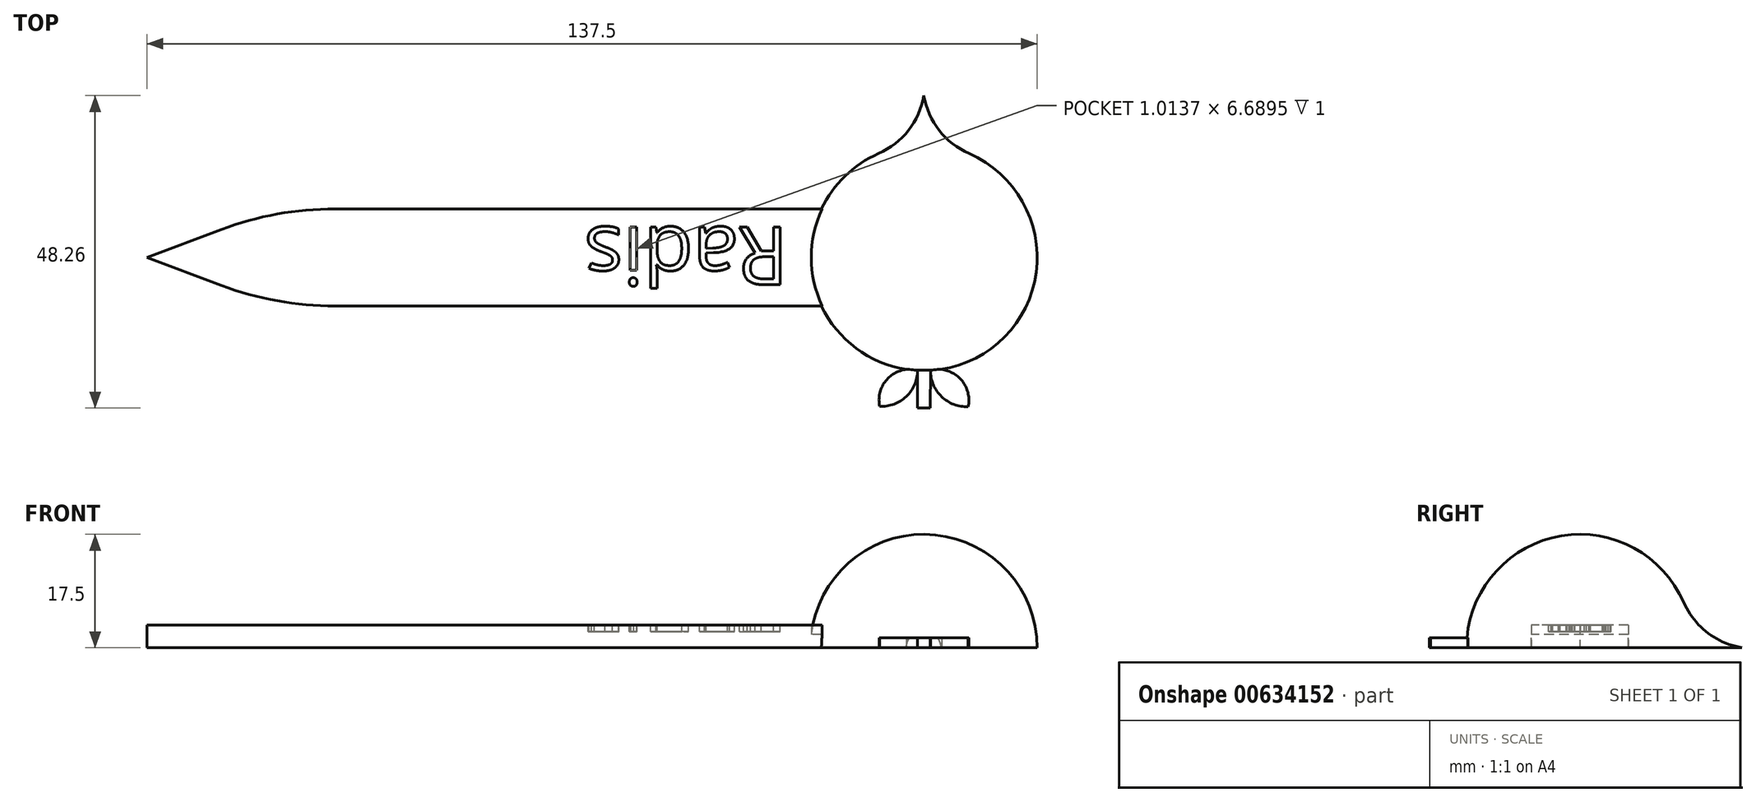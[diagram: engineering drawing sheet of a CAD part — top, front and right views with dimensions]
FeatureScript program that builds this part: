
annotation { "Feature Type Name" : "Feature", "Feature Type Description" : "" }
export const myFeature = defineFeature(function(context is Context, id is Id, definition is map)
    precondition{}
    {
        {
            var Q0;
            Q0=qCreatedBy(makeId("Top.planeOp"),FACE);
            var sketch = newSketch(context, id + "F0", { "sketchPlane" : qUnion([Q0])});
            skLineSegment(sketch, "E0.bottom", {"start": v(20, 7.5) * mm, "end": v(120, 7.5) * mm});
            skLineSegment(sketch, "E0.top", {"start": v(20, -7.5) * mm, "end": v(120, -7.5) * mm});
            skLineSegment(sketch, "E0.left", {"start": v(20, 7.5) * mm, "end": v(20, -7.5) * mm});
            skLineSegment(sketch, "E0.right", {"start": v(120, 7.5) * mm, "end": v(120, -7.5) * mm});
            skLineSegment(sketch, "E1", {"start": v(20, -7.5) * mm, "end": v(0, 0) * mm});
            skPoint(sketch, "E1.endSnap0", {"position": v(20, 0) * mm});
            skLineSegment(sketch, "E2", {"start": v(0, 0) * mm, "end": v(20, 7.5) * mm});
            skSolve(sketch);
        }
        {
            var Q0;
            Q0 = qSketchRegion(id + "F0", true);
            extrude(context, id + "F1", {"entities" : qUnion([Q0]), "depth" : 2 * mm, "offsetDistance" : 25 * mm});
        }
        {
            var Q0;
            Q0=makeQuery(id+"F1.opExtrude","SWEPT_EDGE",EDGE,{"disambiguationData":[OSD([sQuery(id+"F0.wireOp",EDGE,"E0.top"),sQuery(id+"F0.wireOp",EDGE,"E0.left"),sQuery(id+"F0.wireOp",EDGE,"E1")])]});
            var Q1;
            Q1=makeQuery(id+"F1.opExtrude","SWEPT_EDGE",EDGE,{"disambiguationData":[OSD([sQuery(id+"F0.wireOp",EDGE,"E0.bottom"),sQuery(id+"F0.wireOp",EDGE,"E0.left"),sQuery(id+"F0.wireOp",EDGE,"E2")])]});
            fillet(context, id + "F2", {"entities" : qUnion([Q0, Q1]), "radius" : 50 * mm, "tangentPropagation" : true, "allowEdgeOverflow" : false});
        }
        {
            var Q0;
            Q0=makeQuery(id+"F1.opExtrude","CAP_FACE",FACE,{"disambiguationData":[OSD([sQuery(id+"F0.wireOp",EDGE,"E0.bottom"),sQuery(id+"F0.wireOp",EDGE,"E0.top"),sQuery(id+"F0.wireOp",EDGE,"E0.right"),sQuery(id+"F0.wireOp",EDGE,"E1"),sQuery(id+"F0.wireOp",EDGE,"E2")])],"isStart":true});
            var sketch = newSketch(context, id + "F3", { "sketchPlane" : qUnion([Q0])});
            skArc(sketch, "E3", {"start": v(120, 17.5) * mm, "mid": v(102.5, 0) * mm, "end": v(120, -17.5) * mm});
            skLineSegment(sketch, "E4", {"start": v(120, 0) * mm, "end": v(120, -29.85) * mm, "construction": true});
            skArc(sketch, "E5", {"start": v(120, -25) * mm, "mid": v(117.63, -19.63) * mm, "end": v(113, -16.04) * mm});
            skLineSegment(sketch, "E6", {"start": v(120, -25) * mm, "end": v(120, -17.5) * mm});
            skLineSegment(sketch, "E7", {"start": v(120, -17.5) * mm, "end": v(120, 17.5) * mm});
            skSolve(sketch);
        }
        {
            var Q0;
            Q0 = qSketchRegion(id + "F3", true);
            var Q1;
            Q1=sQuery(id+"F3.wireOp",EDGE,"E7");
            revolve(context, id + "F4", {"operationType" : NewBodyOperationType.ADD, "surfaceOperationType" : NewSurfaceOperationType.NEW, "entities" : qUnion([Q0]), "axis" : qUnion([Q1]), "revolveType" : RevolveType.ONE_DIRECTION, "oppositeDirection" : true, "angle" : 180 * degree});
        }
        {
            var Q0;
            Q0=makeQuery(id+"F4.boolean.opBoolean","MERGE",FACE,{"derivedFrom":[makeQuery(id+"F1.opExtrude","CAP_FACE",FACE,{"disambiguationData":[OSD([sQuery(id+"F0.wireOp",EDGE,"E0.bottom"),sQuery(id+"F0.wireOp",EDGE,"E0.top"),sQuery(id+"F0.wireOp",EDGE,"E0.right"),sQuery(id+"F0.wireOp",EDGE,"E1"),sQuery(id+"F0.wireOp",EDGE,"E2")])],"isStart":true}),makeQuery(id+"F4.opRevolve","CAP_FACE",FACE,{"disambiguationData":[OSD([sQuery(id+"F3.wireOp",EDGE,"E3"),sQuery(id+"F3.wireOp",EDGE,"E5"),sQuery(id+"F3.wireOp",EDGE,"E6"),sQuery(id+"F3.wireOp",EDGE,"E7")])],"isStart":true})]});
            var sketch = newSketch(context, id + "F5", { "sketchPlane" : qUnion([Q0])});
            skLineSegment(sketch, "E8", {"start": v(120, 27.39) * mm, "end": v(120.1, -8.4) * mm, "construction": true});
            skLineSegment(sketch, "E9", {"start": v(120.01, 23.26) * mm, "end": v(119.01, 23.25) * mm});
            skLineSegment(sketch, "E10", {"start": v(119.01, 23.25) * mm, "end": v(119.03, 17.47) * mm});
            skArc(sketch, "E11", {"start": v(119.03, 17.47) * mm, "mid": v(117.3, 21.5) * mm, "end": v(113.18, 23) * mm});
            skArc(sketch, "E12", {"start": v(113.18, 23) * mm, "mid": v(113.98, 19.23) * mm, "end": v(117.3, 17.3) * mm});
            skLineSegment(sketch, "E13.MirrorCS", {"start": v(120.01, 23.26) * mm, "end": v(121.01, 23.26) * mm});
            skLineSegment(sketch, "E14.MirrorCS", {"start": v(121.01, 23.26) * mm, "end": v(121.03, 17.48) * mm});
            skArc(sketch, "E15.MirrorCS", {"start": v(121.03, 17.48) * mm, "mid": v(122.74, 21.5) * mm, "end": v(126.85, 23.04) * mm});
            skArc(sketch, "E16.MirrorCS", {"start": v(126.85, 23.04) * mm, "mid": v(126.07, 19.27) * mm, "end": v(122.75, 17.3) * mm});
            skLineSegment(sketch, "E17", {"start": v(117.3, 17.3) * mm, "end": v(122.75, 17.3) * mm});
            skSolve(sketch);
        }
        {
            var Q0;
            Q0 = qSketchRegion(id + "F5", true);
            var Q1;
            Q1=makeQuery(id+"F1.opExtrude","CAP_FACE",FACE,{"disambiguationData":[OSD([sQuery(id+"F0.wireOp",EDGE,"E0.bottom"),sQuery(id+"F0.wireOp",EDGE,"E0.top"),sQuery(id+"F0.wireOp",EDGE,"E0.right"),sQuery(id+"F0.wireOp",EDGE,"E1"),sQuery(id+"F0.wireOp",EDGE,"E2")])],"isStart":false});
            extrude(context, id + "F6", {"entities" : qUnion([Q0, Q1]), "operationType" : NewBodyOperationType.ADD, "oppositeDirection" : true, "depth" : 1.5 * mm, "offsetDistance" : 25 * mm});
        }
        {
            var Q0;
            Q0=makeQuery(id+"F6.opExtrude","CAP_FACE",FACE,{"disambiguationData":[OSD([sQuery(id+"F0.wireOp",EDGE,"E0.bottom"),sQuery(id+"F0.wireOp",EDGE,"E0.top"),sQuery(id+"F0.wireOp",EDGE,"E0.right"),sQuery(id+"F0.wireOp",EDGE,"E1"),sQuery(id+"F0.wireOp",EDGE,"E2")])],"isStart":false});
            var sketch = newSketch(context, id + "F7", { "sketchPlane" : qUnion([Q0])});
            skText(sketch, "E18", { "text": "Radis", "fontName": "OpenSans-Regular.ttf"});
            const initialGuessF7  = {"E18": [0.09904, 0.0047, -1, 0, 0.009]};
            skSetInitialGuess(sketch, initialGuessF7);
            skSolve(sketch);
        }
        {
            var Q0;
            Q0 = qSketchRegion(id + "F7", true);
            var Q1;
            Q1 = qConstructionFilter(qBodyType(qCreatedBy(id + "F7" ,EDGE), BodyType.WIRE), ConstructionObject.NO);
            extrude(context, id + "F8", {"entities" : qUnion([Q0]), "operationType" : NewBodyOperationType.REMOVE, "surfaceEntities" : qUnion([Q1]), "oppositeDirection" : true, "depth" : 1 * mm, "offsetDistance" : 25 * mm});
        }
    });
